annotation { "Feature Type Name" : "Feature", "Feature Type Description" : "" }
export const myFeature = defineFeature(function(context is Context, id is Id, definition is map)
    precondition{}
    {
        {
            var Q0;
            Q0=qCreatedBy(makeId("Front.planeOp"),FACE);
            var sketch = newSketch(context, id + "F0", { "sketchPlane" : qUnion([Q0])});
            skLineSegment(sketch, "E0.bottom", {"start": v(-50.8, 25.4) * mm, "end": v(50.8, 25.4) * mm});
            skLineSegment(sketch, "E0.top", {"start": v(-50.8, -25.4) * mm, "end": v(50.8, -25.4) * mm});
            skLineSegment(sketch, "E0.left", {"start": v(-50.8, 25.4) * mm, "end": v(-50.8, -25.4) * mm});
            skLineSegment(sketch, "E0.right", {"start": v(50.8, 25.4) * mm, "end": v(50.8, -25.4) * mm});
            skPoint(sketch, "E0.middle", {"position": v(0, 0) * mm});
            skSolve(sketch);
        }
        {
            var Q0;
            Q0 = qSketchRegion(id + "F3", true);
            var Q1;
            Q1 = qSketchRegion(id + "F0", true);
            extrude(context, id + "F1", {"entities" : qUnion([Q0, Q1]), "depth" : 9.52 * mm, "offsetDistance" : 25.4 * mm});
        }
        {
            var Q0;
            Q0=makeQuery(id+"F1.opExtrude","CAP_FACE",FACE,{"disambiguationData":[OSD([sQuery(id+"F0.wireOp",EDGE,"E0.bottom"),sQuery(id+"F0.wireOp",EDGE,"E0.top"),sQuery(id+"F0.wireOp",EDGE,"E0.left"),sQuery(id+"F0.wireOp",EDGE,"E0.right")])],"isStart":false});
            fillet(context, id + "F2", {"entities" : qUnion([Q0]), "radius" : 3.8 * mm, "tangentPropagation" : true, "allowEdgeOverflow" : false});
        }
        {
            var Q0;
            Q0=makeQuery(id+"F1.opExtrude","CAP_FACE",FACE,{"disambiguationData":[OSD([sQuery(id+"F0.wireOp",EDGE,"E0.bottom"),sQuery(id+"F0.wireOp",EDGE,"E0.top"),sQuery(id+"F0.wireOp",EDGE,"E0.left"),sQuery(id+"F0.wireOp",EDGE,"E0.right")])],"isStart":false});
            var sketch = newSketch(context, id + "F3", { "sketchPlane" : qUnion([Q0])});
            skText(sketch, "E1", { "text": "Arnulfo Morales", "fontName": "AllertaStencil-Regular.ttf"});
            skPoint(sketch, "E1.secondSnap0", {"position": v(47, 0) * mm});
            skPoint(sketch, "E2", {"position": v(0, 21.6) * mm});
            const initialGuessF3  = {"E1": [-0.0473, 0, 1, 0, 0.00833]};
            skSetInitialGuess(sketch, initialGuessF3);
            skSolve(sketch);
        }
        {
            var Q0;
            Q0 = qSketchRegion(id + "F3", true);
            extrude(context, id + "F4", {"entities" : qUnion([Q0]), "operationType" : NewBodyOperationType.REMOVE, "oppositeDirection" : true, "depth" : 3.17 * mm, "offsetDistance" : 25.4 * mm});
        }
        {
            var Q0;
            Q0=makeQuery(id+"F1.opExtrude","CAP_FACE",FACE,{"disambiguationData":[OSD([sQuery(id+"F0.wireOp",EDGE,"E0.bottom"),sQuery(id+"F0.wireOp",EDGE,"E0.top"),sQuery(id+"F0.wireOp",EDGE,"E0.left"),sQuery(id+"F0.wireOp",EDGE,"E0.right")])],"isStart":false});
            var sketch = newSketch(context, id + "F5", { "sketchPlane" : qUnion([Q0])});
            skPoint(sketch, "E3.4.internal.snap0", {"position": v(-28.71, -3.64) * mm});
            skFitSpline(sketch, "E3", {"points": [v(-30.6, -10.18) * mm, v(-30.64, -8.12) * mm, v(-30.03, -5.97) * mm, v(-29.06, -4.28) * mm, v(-28.71, -3.92) * mm, v(-27.92, -4.88) * mm, v(-27.16, -6.28) * mm, v(-26.77, -7.97) * mm, v(-26.74, -10.3) * mm, v(-26.98, -10.27) * mm, v(-30.45, -10.22) * mm, v(-30.6, -10.18) * mm]});
            skFitSpline(sketch, "E4", {"points": [v(-26.37, -10.17) * mm, v(-25.1, -8.66) * mm, v(-23.42, -7.53) * mm, v(-21.99, -6.98) * mm, v(-21.08, -6.83) * mm, v(-21.08, -7.07) * mm], "startDerivative": vector(4.56, 6.2) * mm, "endDerivative": vector(-0.91, -3.32) * mm});
            skFitSpline(sketch, "E5", {"points": [v(-26.37, -10.17) * mm, v(-21.91, -10.3) * mm], "startDerivative": vector(4.46, -0.13) * mm, "endDerivative": vector(4.46, -0.13) * mm});
            skFitSpline(sketch, "E6", {"points": [v(-21.91, -10.3) * mm, v(-21.34, -8.84) * mm, v(-21.08, -7.07) * mm, v(-21.05, -6.97) * mm], "startDerivative": vector(1.51, 2.94) * mm, "endDerivative": vector(0.23, 0.57) * mm});
            skFitSpline(sketch, "E7", {"points": [v(-30.96, -10.18) * mm, v(-32.64, -8.4) * mm, v(-34.94, -7.07) * mm, v(-36.2, -6.83) * mm, v(-36.24, -6.86) * mm, v(-36.27, -7.37) * mm, v(-36.07, -8.64) * mm, v(-35.42, -10.18) * mm, v(-35.28, -10.19) * mm, v(-31.57, -10.19) * mm, v(-31.31, -10.19) * mm, v(-30.96, -10.18) * mm]});
            skLineSegment(sketch, "E8", {"start": v(-35.12, -10.77) * mm, "end": v(-22.27, -10.77) * mm});
            skLineSegment(sketch, "E9", {"start": v(-35.12, -10.77) * mm, "end": v(-34.78, -11.35) * mm});
            skLineSegment(sketch, "E10", {"start": v(-34.78, -11.35) * mm, "end": v(-22.65, -11.4) * mm});
            skLineSegment(sketch, "E11", {"start": v(-22.65, -11.4) * mm, "end": v(-22.26, -10.85) * mm});
            skLineSegment(sketch, "E12", {"start": v(-34.2, -12.01) * mm, "end": v(-23.16, -12.01) * mm});
            skLineSegment(sketch, "E13", {"start": v(-23.16, -12.01) * mm, "end": v(-23.7, -12.57) * mm});
            skLineSegment(sketch, "E14", {"start": v(-23.7, -12.57) * mm, "end": v(-33.66, -12.55) * mm});
            skLineSegment(sketch, "E15", {"start": v(-33.66, -12.55) * mm, "end": v(-34.2, -12.01) * mm});
            skLineSegment(sketch, "E16", {"start": v(-32.83, -13.11) * mm, "end": v(-29.83, -13.08) * mm});
            skLineSegment(sketch, "E17", {"start": v(-29.83, -13.08) * mm, "end": v(-29.76, -14.39) * mm});
            skLineSegment(sketch, "E18", {"start": v(-29.76, -14.39) * mm, "end": v(-30.5, -14.3) * mm});
            skLineSegment(sketch, "E19", {"start": v(-30.5, -14.3) * mm, "end": v(-31.47, -13.98) * mm});
            skLineSegment(sketch, "E20", {"start": v(-31.47, -13.98) * mm, "end": v(-32.55, -13.38) * mm});
            skLineSegment(sketch, "E21", {"start": v(-32.55, -13.38) * mm, "end": v(-32.83, -13.1) * mm});
            skLineSegment(sketch, "E22", {"start": v(-29.65, -13.13) * mm, "end": v(-28.71, -14.44) * mm});
            skLineSegment(sketch, "E23", {"start": v(-28.71, -14.44) * mm, "end": v(-28.4, -14.2) * mm});
            skLineSegment(sketch, "E24", {"start": v(-28.4, -14.2) * mm, "end": v(-27.7, -13.17) * mm});
            skLineSegment(sketch, "E25", {"start": v(-27.7, -13.17) * mm, "end": v(-27.7, -13.1) * mm});
            skLineSegment(sketch, "E26", {"start": v(-27.7, -13.1) * mm, "end": v(-29.65, -13.13) * mm});
            skLineSegment(sketch, "E27", {"start": v(-27.52, -13.12) * mm, "end": v(-24.65, -13.12) * mm});
            skLineSegment(sketch, "E28", {"start": v(-24.65, -13.12) * mm, "end": v(-25.32, -13.72) * mm});
            skLineSegment(sketch, "E29", {"start": v(-25.32, -13.72) * mm, "end": v(-26.92, -14.34) * mm});
            skLineSegment(sketch, "E30", {"start": v(-26.92, -14.34) * mm, "end": v(-27.6, -14.36) * mm});
            skLineSegment(sketch, "E31", {"start": v(-27.6, -14.36) * mm, "end": v(-27.52, -13.1) * mm});
            skLineSegment(sketch, "E32", {"start": v(-22.27, -10.77) * mm, "end": v(-22.26, -10.85) * mm});
            skLineSegment(sketch, "E33", {"start": v(-27.52, -13.12) * mm, "end": v(-27.52, -13.12) * mm});
            skSolve(sketch);
        }
        {
            var Q0;
            Q0 = qSketchRegion(id + "F5", true);
            extrude(context, id + "F6", {"entities" : qUnion([Q0]), "depth" : 3.17 * mm, "offsetDistance" : 25.4 * mm});
        }
    });